# Revit family: Bath-Drop_In-VibrAcoustic-KOHLER-Fountainhead-K-EX24430T_1
name_source: partatom
category: Plumbing Fixtures
units: mm (PartAtom-declared; Revit-internal decimal feet)

## family parameters
Cut with Voids When Loaded = No
Host = Face
Maintain Annotation Orientation = No
OmniClass Number = 23.31.15.00
OmniClass Title = Bathtubs
Part Type = Normal
Room Calculation Point = No
Round Connector Dimension = Use Diameter
Shared = No

## types (1)
- 0-White
    ADA Compliant = No
    Amplifer Electrical Connector = Amplifer Electrical Connector
    Apparent Load = 2200 VA
    Assembly Code = D2010500
    Blower Electrical Connector = Blower Electrical Connector
    CW Connection = No
    Cold Water Inlet = Cold Water Inlet
    Date Modified = 7/19/2022
    Default Elevation = 0"
    Description = 2.0 VAB BATH, CLOUD (EXQ)
    Drain Included = Yes
    Electrical Connector = Yes
    Electrical Note = Two Dedicated Circuits Required
    Finish = KOHLER-Acrylic-0-White
    HW Connection = No
    Heater Electrical Connector = Heater Electrical Connector
    Height = 29 11/16"
    Hot Water Inlet = Hot Water Inlet
    Length = 86 1/2"
    Manufacturer = Kohler Co.
    Master Format 2014 = 22 41 19
    Master Format 2014 Name = Residential Bathtubs
    Material = Acrylic
    Model = K-EX24430T-XVBW-0
    Product Name = Fountainhead
    Pump Electrical Connector = Pump Electrical Connector
    Type = 1
    URL = http://www.kohler.com.cn
    Vent Connection = No
    Voltage = 220 V
    Waste Connection = Yes
    Waste Water Outlet = Waste Water Outlet
    WaterSense Certified = No
    Width = 47 1/8"

## geometry (parser evidence)
native form markers: Sweep x5
no freeform markers — native parametric forms only
